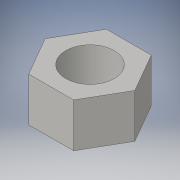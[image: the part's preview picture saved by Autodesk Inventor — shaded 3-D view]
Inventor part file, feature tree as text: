
AUTODESK INVENTOR PART (.ipt)
format: ipt  version: 2016 (Build 200138000, 138)  size: 94,208 bytes
history: native  units: in
note: dims shown in document units (in); Inventor stores cm internally (conversion verified against a paired STEP export)
features: extrude x1, sketch x1
ambient origin geometry x8: Origin, YZ Plane, XZ Plane, XY Plane, X Axis, Y Axis, Z Axis, Center Point
bodies: Solid1 (feature_tree)
feature tree (2):
  extrude  "Extrusion1"  Depth=0.34in
  sketch  "Sketch1"  dims[d0=0.6in d1=0.375in d2=0.34in d3=0.0in]
